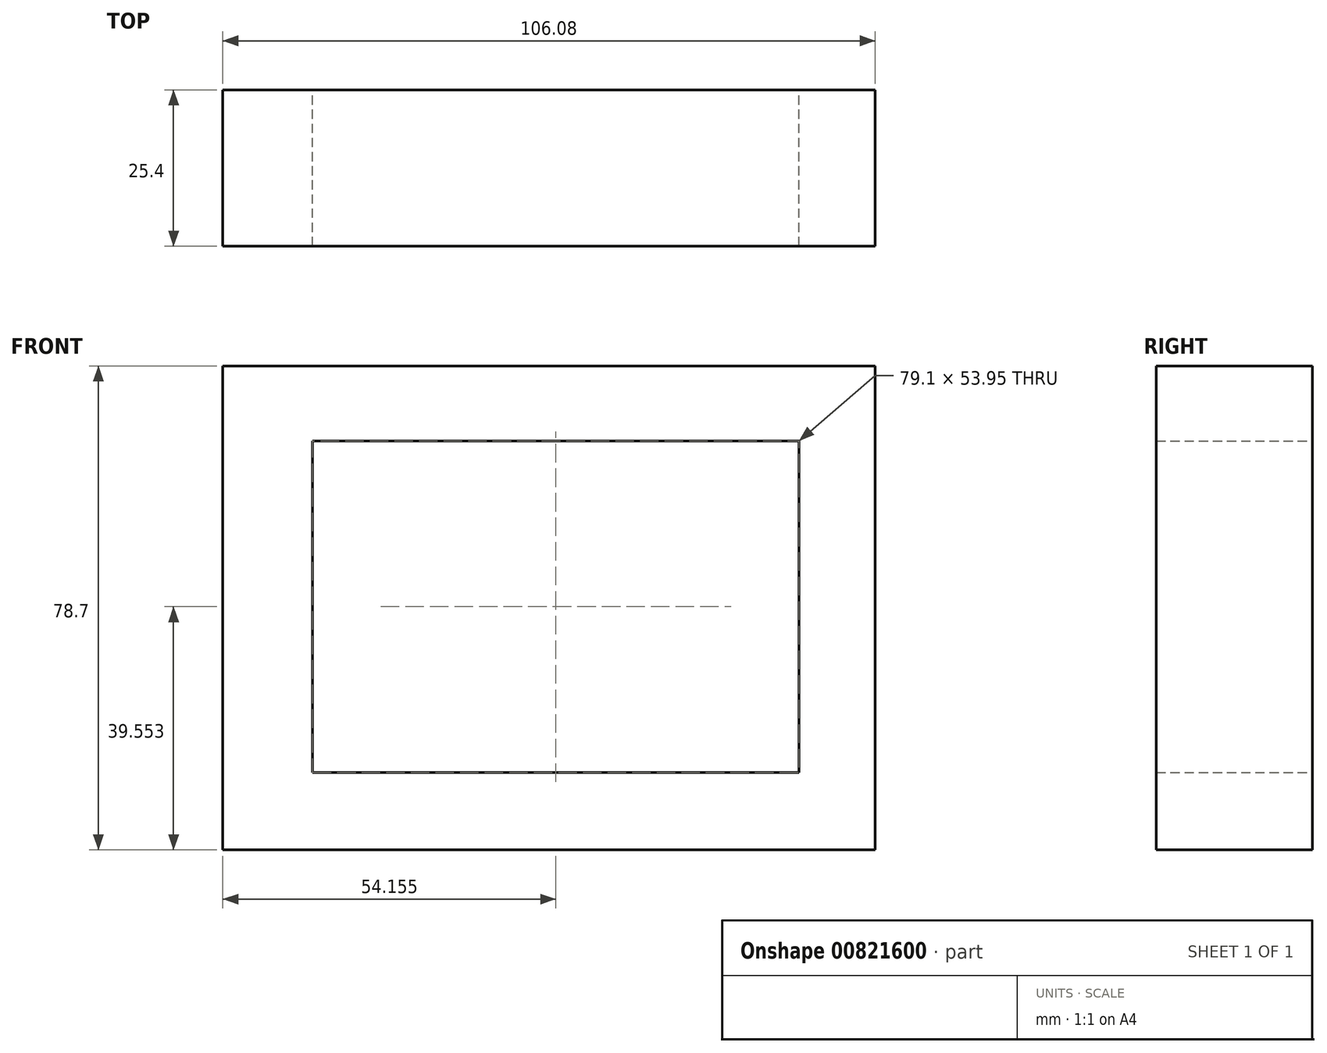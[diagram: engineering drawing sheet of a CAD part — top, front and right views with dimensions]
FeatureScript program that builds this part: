
annotation { "Feature Type Name" : "Feature", "Feature Type Description" : "" }
export const myFeature = defineFeature(function(context is Context, id is Id, definition is map)
    precondition{}
    {
        {
            var Q0;
            Q0=qCreatedBy(makeId("Front.planeOp"),FACE);
            var sketch = newSketch(context, id + "F0", { "sketchPlane" : qUnion([Q0])});
            skLineSegment(sketch, "E0.bottom", {"start": v(-50.2, 36.5) * mm, "end": v(55.88, 36.5) * mm});
            skLineSegment(sketch, "E0.top", {"start": v(-50.2, -42.19) * mm, "end": v(55.88, -42.19) * mm});
            skLineSegment(sketch, "E0.left", {"start": v(-50.2, 36.5) * mm, "end": v(-50.2, -42.19) * mm});
            skLineSegment(sketch, "E0.right", {"start": v(55.88, 36.5) * mm, "end": v(55.88, -42.19) * mm});
            skLineSegment(sketch, "E1.bottom", {"start": v(-35.6, 24.34) * mm, "end": v(43.5, 24.34) * mm});
            skLineSegment(sketch, "E1.top", {"start": v(-35.6, -29.61) * mm, "end": v(43.5, -29.61) * mm});
            skLineSegment(sketch, "E1.left", {"start": v(-35.6, 24.34) * mm, "end": v(-35.6, -29.61) * mm});
            skLineSegment(sketch, "E1.right", {"start": v(43.5, 24.34) * mm, "end": v(43.5, -29.61) * mm});
            skSolve(sketch);
        }
        {
            var Q0;
            Q0=makeQuery(id+"F0.imprint","IMPRINT",FACE,{"disambiguationData":[TD([[makeQuery(id+"F0.imprint","IMPRINT",EDGE,{"derivedFrom":sQuery(id+"F0.wireOp",EDGE,"E0.bottom")}),-1.0]])]});
            extrude(context, id + "F1", {"entities" : qUnion([Q0]), "depth" : 25.4 * mm, "offsetDistance" : 25.4 * mm});
        }
    });
